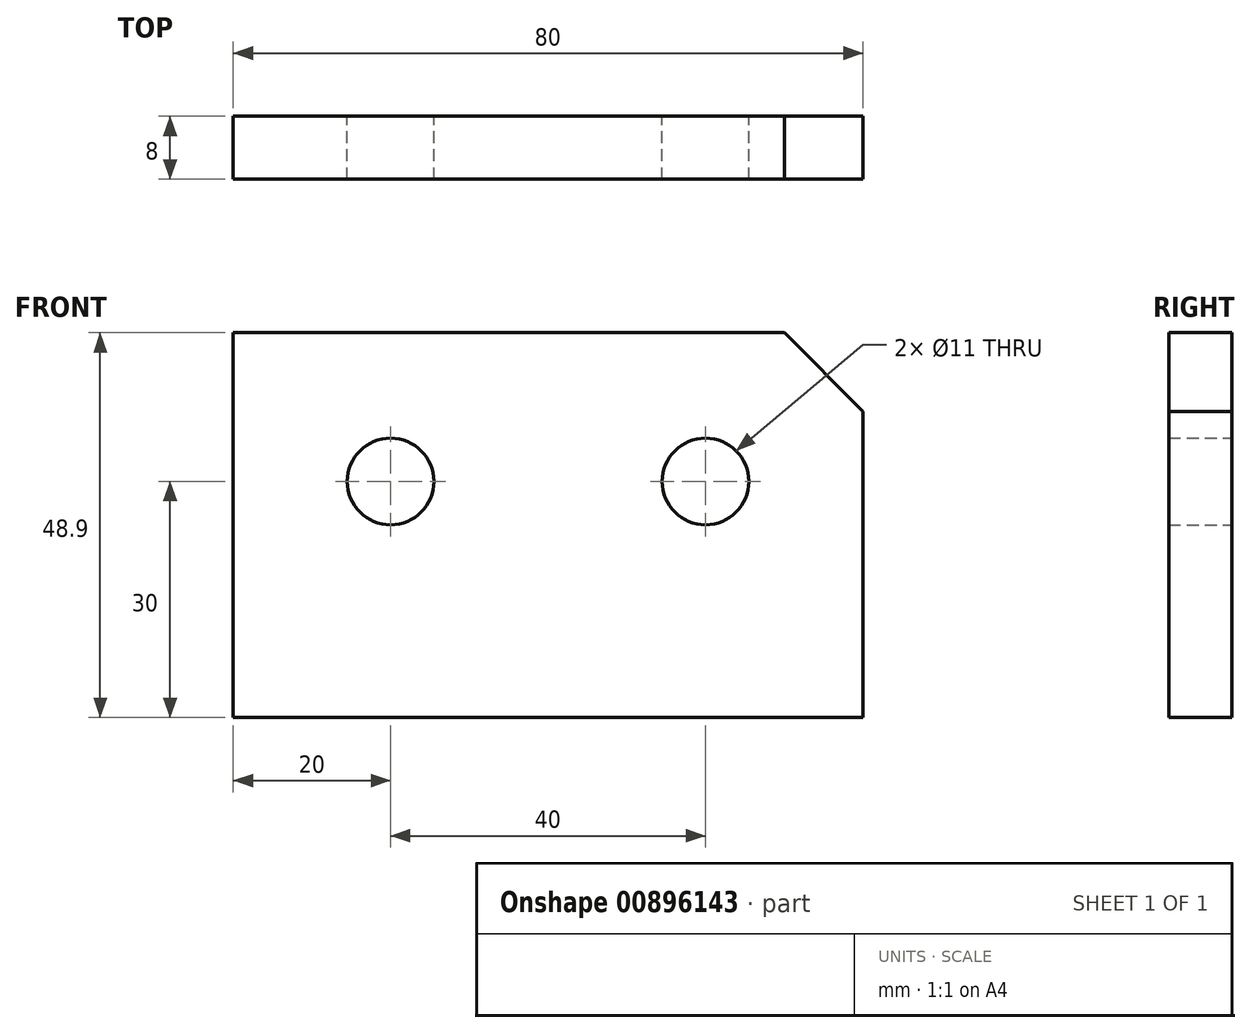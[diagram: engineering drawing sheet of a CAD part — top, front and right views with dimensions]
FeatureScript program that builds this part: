
annotation { "Feature Type Name" : "Feature", "Feature Type Description" : "" }
export const myFeature = defineFeature(function(context is Context, id is Id, definition is map)
    precondition{}
    {
        {
            var Q0;
            Q0=qCreatedBy(makeId("Front.planeOp"),FACE);
            var sketch = newSketch(context, id + "F0", { "sketchPlane" : qUnion([Q0])});
            skLineSegment(sketch, "E0.bottom", {"start": v(40, 24.45) * mm, "end": v(-40, 24.45) * mm});
            skLineSegment(sketch, "E0.top", {"start": v(40, -24.45) * mm, "end": v(-40, -24.45) * mm});
            skLineSegment(sketch, "E0.left", {"start": v(40, 24.45) * mm, "end": v(40, -24.45) * mm});
            skLineSegment(sketch, "E0.right", {"start": v(-40, 24.45) * mm, "end": v(-40, -24.45) * mm});
            skPoint(sketch, "E0.middle", {"position": v(0, 0) * mm});
            skCircle(sketch, "E1", {"center": v(-20, 5.55) * mm, "radius": 5.5 * mm});
            skCircle(sketch, "E2", {"center": v(20, 5.55) * mm, "radius": 5.5 * mm});
            skSolve(sketch);
        }
        {
            var Q0;
            Q0=makeQuery(id+"F0.imprint","IMPRINT",FACE,{"disambiguationData":[TD([[makeQuery(id+"F0.imprint","IMPRINT",EDGE,{"derivedFrom":sQuery(id+"F0.wireOp",EDGE,"E0.bottom")}),1.0]])]});
            extrude(context, id + "F1", {"entities" : qUnion([Q0]), "depth" : 8 * mm, "offsetDistance" : 25 * mm});
        }
        {
            var Q0;
            Q0=makeQuery(id+"F1.opExtrude","SWEPT_EDGE",EDGE,{"disambiguationData":[OSD([sQuery(id+"F0.wireOp",EDGE,"E0.bottom"),sQuery(id+"F0.wireOp",EDGE,"E0.left")])]});
            chamfer(context, id + "F2", {"entities" : qUnion([Q0]), "width" : 10 * mm, "tangentPropagation" : true});
        }
    });
